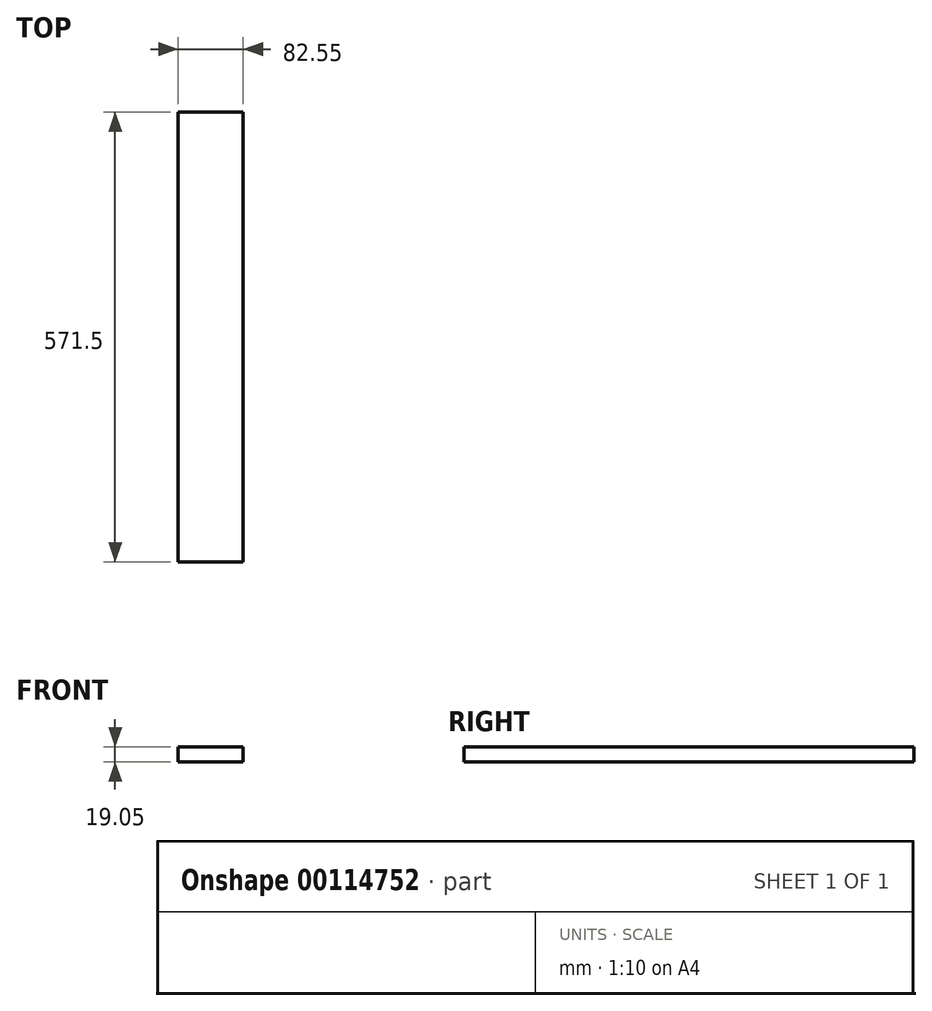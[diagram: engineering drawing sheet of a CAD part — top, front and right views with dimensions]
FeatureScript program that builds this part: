
annotation { "Feature Type Name" : "Feature", "Feature Type Description" : "" }
export const myFeature = defineFeature(function(context is Context, id is Id, definition is map)
    precondition{}
    {
        {
            var Q0;
            Q0=qCreatedBy(makeId("Top.planeOp"),FACE);
            var sketch = newSketch(context, id + "F0", { "sketchPlane" : qUnion([Q0])});
            skLineSegment(sketch, "E0.bottom", {"start": v(0, 0) * mm, "end": v(82.55, 0) * mm});
            skLineSegment(sketch, "E0.top", {"start": v(0, 571.5) * mm, "end": v(82.55, 571.5) * mm});
            skLineSegment(sketch, "E0.left", {"start": v(0, 0) * mm, "end": v(0, 571.5) * mm});
            skLineSegment(sketch, "E0.right", {"start": v(82.55, 0) * mm, "end": v(82.55, 571.5) * mm});
            skSolve(sketch);
        }
        {
            var Q0;
            Q0=qSketchRegion(id+"F0",true);
            extrude(context, id + "F1", {"entities" : qUnion([Q0]), "depth" : 19.05 * mm});
        }
    });
